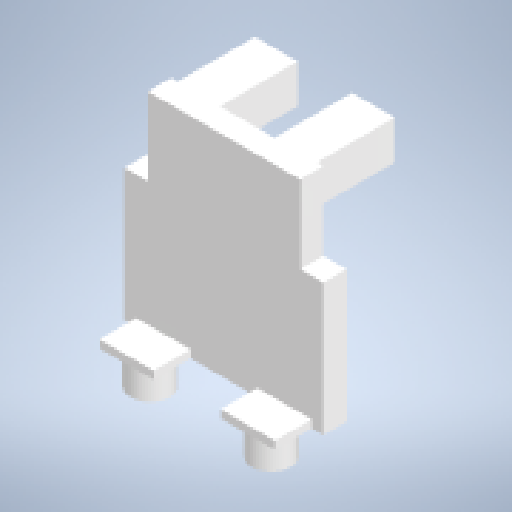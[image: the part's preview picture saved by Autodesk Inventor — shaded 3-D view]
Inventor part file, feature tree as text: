
AUTODESK INVENTOR PART (.ipt)
format: ipt  version: 2025 (Build 290162010, 162A)  size: 217,600 bytes
history: native  units: mm
features: extrude x4, sketch x4
ambient origin geometry x8: Origin, YZ Plane, XZ Plane, XY Plane, X Axis, Y Axis, Z Axis, Center Point
bodies: Volumenkörper1 (feature_tree)
feature tree (8):
  extrude  "Extrusion1"  Depth=3.0mm TaperAngle=0.0deg
  extrude  "Extrusion2"  Depth=5.0mm
  sketch  "Skizze5"  dims[d31=4.0mm d32=0.0mm d43=7.0mm]
  extrude  "Extrusion4"  Depth=7.0mm
  extrude  "Extrusion5"  Depth=5.0mm
  sketch  "Skizze1"  dims[d1=27.0mm d7=3.0mm d8=0.0mm]
  sketch  "Skizze3"  dims[d9=25.6mm d29=5.0mm]
  sketch  "Skizze6"  dims[d50=10.0mm d51=0.0mm d54=5.0mm d55=18.0mm d56=3.0mm d57=10.0mm d58=3.0mm d59=10.0mm d60=5.0mm d62=5.0mm d64=5.0mm d65=7.0mm d66=1.0mm d67=7.0mm d68=1.0mm d69=7.75mm d70=0.0mm d71=5.0mm d72=0.0mm d73=1.0mm]
